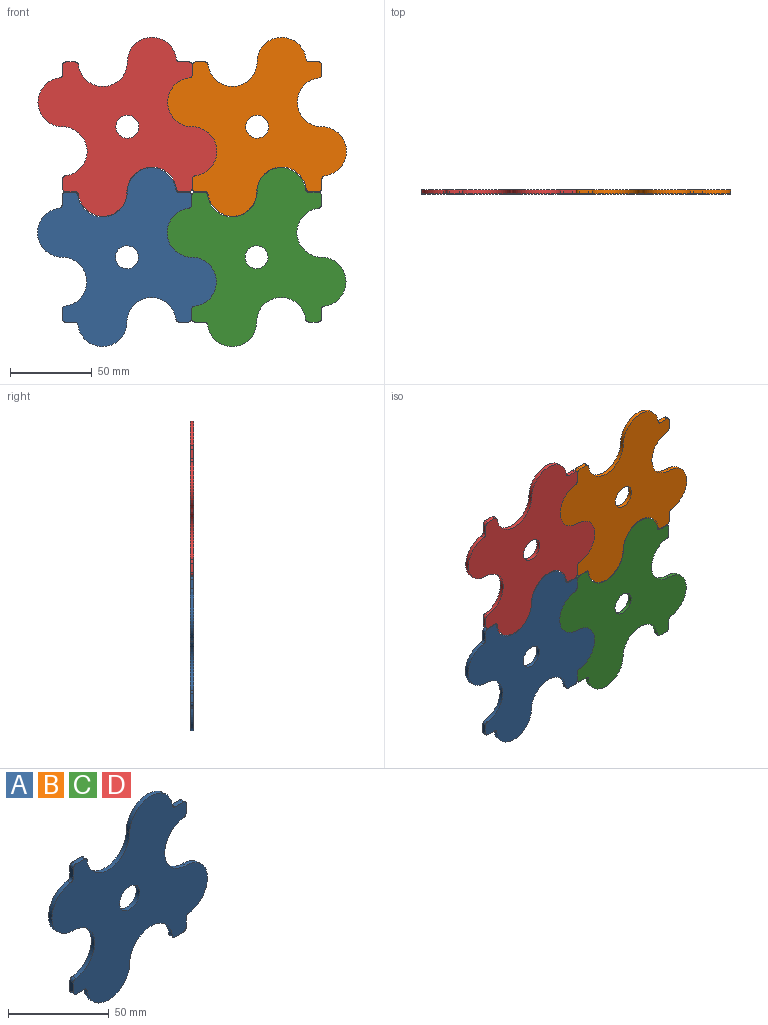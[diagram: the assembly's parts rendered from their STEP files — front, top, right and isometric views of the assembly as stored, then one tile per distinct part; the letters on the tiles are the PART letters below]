
ASSEMBLY  parts=4 mates=2
PART A: 31 faces, bbox 109.2x2.4x109.2 mm
  f0: cylinder r=15mm len=29.9mm, axis (0,-1,0), area 107.9mm2, adj f1,f27,f28,f30
  f1: cylinder r=15mm len=29.9mm, axis (0,-1,0), area 107.9mm2, adj f0,f2,f28,f30
  f2: cylinder r=2mm len=2.38mm, axis (0,-1,0), area 6.9mm2, adj f1,f3,f28,f30
  f3: plane 5.72x2.38mm, normal (1,0,0), area 13.6mm2, adj f2,f4,f28,f30
  f4: cylinder r=2mm len=2.38mm, axis (0,-1,0), area 7.5mm2, adj f3,f5,f28,f30
  f5: plane 5.72x2.38mm, normal (0,0,-1), area 13.6mm2, adj f4,f6,f28,f30
  f6: cylinder r=2mm len=2.38mm, axis (0,-1,0), area 6.9mm2, adj f5,f7,f28,f30
  f7: cylinder r=15mm len=29.9mm, axis (0,-1,0), area 107.9mm2, adj f6,f8,f28,f30
  f8: cylinder r=15mm len=29.9mm, axis (0,-1,0), area 107.9mm2, adj f7,f9,f28,f30
  f9: cylinder r=2mm len=2.38mm, axis (0,-1,0), area 6.9mm2, adj f8,f10,f28,f30
  f10: plane 5.72x2.38mm, normal (0,0,-1), area 13.6mm2, adj f9,f11,f28,f30
  f11: cylinder r=2mm len=2.38mm, axis (0,-1,0), area 7.5mm2, adj f10,f12,f28,f30
  f12: plane 5.72x2.38mm, normal (-1,0,0), area 13.6mm2, adj f11,f13,f28,f30
  f13: cylinder r=2mm len=2.38mm, axis (0,-1,0), area 6.9mm2, adj f12,f14,f28,f30
  f14: cylinder r=15mm len=29.9mm, axis (0,-1,0), area 107.9mm2, adj f13,f15,f28,f30
  f15: cylinder r=15mm len=29.9mm, axis (0,-1,0), area 107.9mm2, adj f14,f16,f28,f30
  f16: cylinder r=2mm len=2.38mm, axis (0,-1,0), area 6.9mm2, adj f15,f17,f28,f30
  f17: plane 5.72x2.38mm, normal (-1,0,0), area 13.6mm2, adj f16,f18,f28,f30
  f18: cylinder r=2mm len=2.38mm, axis (0,-1,0), area 7.5mm2, adj f17,f19,f28,f30
  f19: plane 5.72x2.38mm, normal (0,0,1), area 13.6mm2, adj f18,f20,f28,f30
  f20: cylinder r=2mm len=2.38mm, axis (0,-1,0), area 6.9mm2, adj f19,f21,f28,f30
  f21: cylinder r=15mm len=29.9mm, axis (0,-1,0), area 107.9mm2, adj f20,f22,f28,f30
  f22: cylinder r=15mm len=29.9mm, axis (0,-1,0), area 107.9mm2, adj f21,f23,f28,f30
  f23: cylinder r=2mm len=2.38mm, axis (0,-1,0), area 6.9mm2, adj f22,f24,f28,f30
  f24: plane 5.72x2.38mm, normal (0,0,1), area 13.6mm2, adj f23,f25,f28,f30
  f25: cylinder r=2mm len=2.38mm, axis (0,-1,0), area 7.5mm2, adj f24,f26,f28,f30
  f26: plane 5.72x2.38mm, normal (1,0,0), area 13.6mm2, adj f25,f27,f28,f30
  f27: cylinder r=2mm len=2.38mm, axis (0,-1,0), area 6.9mm2, adj f0,f26,f28,f30
  f28: plane 109.2x109.2mm, normal (0,1,0), area 6114.6mm2, adj f0,f1,f2,f3,f4,f5,f6,f7
  f29: cylinder r=7mm len=14mm, axis (0,-1,0), area 104.7mm2, adj f28,f30
  f30: plane 109.2x109.2mm, normal (0,-1,0), area 6114.6mm2, adj f0,f1,f2,f3,f4,f5,f6,f7
PART B: same geometry as A
PART C: same geometry as A
PART D: same geometry as A
PLACE A t=(23.26,0,-0.55)mm
PLACE B t=(102.76,0,79.08)mm
PLACE C t=(102.46,0,-0.55)mm
PLACE D t=(23.56,0,79.08)mm
MATE planar A.f1 <-> C.f14  axis (0,-1,0) through (62.86,0,-15.55)mm
MATE planar D.f1 <-> B.f14  axis (0,-1,0) through (63.16,0,64.08)mm
